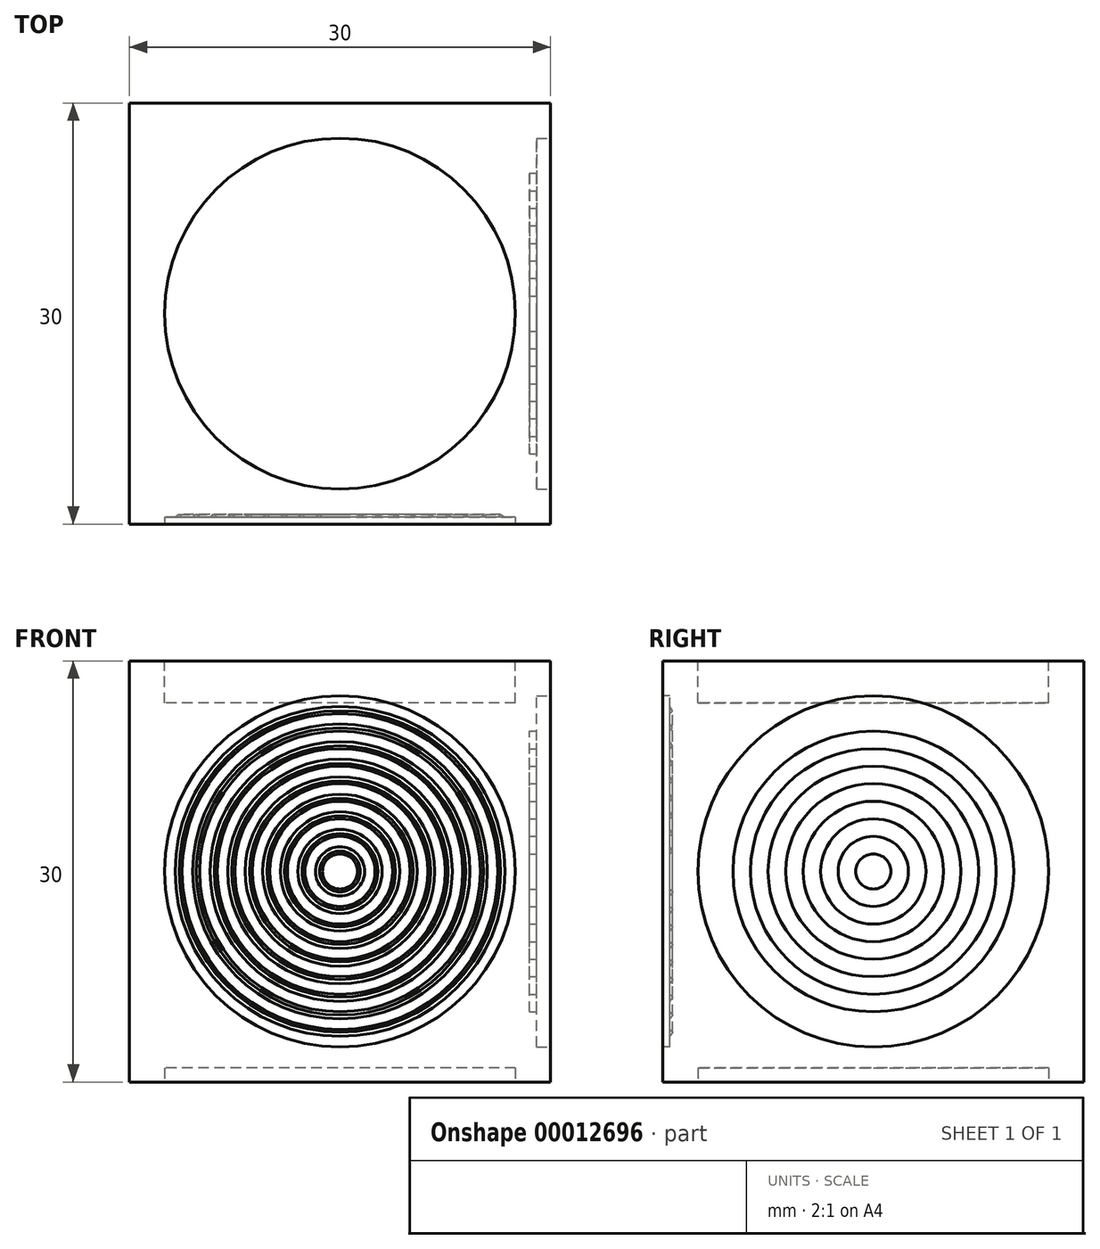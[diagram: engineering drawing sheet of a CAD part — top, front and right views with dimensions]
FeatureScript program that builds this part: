
annotation { "Feature Type Name" : "Feature", "Feature Type Description" : "" }
export const myFeature = defineFeature(function(context is Context, id is Id, definition is map)
    precondition{}
    {
        {
            var Q0;
            Q0=qCreatedBy(makeId("Top.planeOp"),FACE);
            var sketch = newSketch(context, id + "F0", { "sketchPlane" : qUnion([Q0])});
            skLineSegment(sketch, "E0.bottom", {"start": v(-30, 0) * mm, "end": v(0, 0) * mm});
            skLineSegment(sketch, "E0.top", {"start": v(-30, 30) * mm, "end": v(0, 30) * mm});
            skLineSegment(sketch, "E0.left", {"start": v(-30, 0) * mm, "end": v(-30, 30) * mm});
            skLineSegment(sketch, "E0.right", {"start": v(0, 0) * mm, "end": v(0, 30) * mm});
            skSolve(sketch);
        }
        {
            var Q0;
            Q0 = qSketchRegion(id + "F0", true);
            extrude(context, id + "F1", {"entities" : qUnion([Q0]), "depth" : 30 * mm});
        }
        {
            var Q0;
            Q0=qCreatedBy(makeId("Top.planeOp"),FACE);
            var sketch = newSketch(context, id + "F2", { "sketchPlane" : qUnion([Q0])});
            skCircle(sketch, "E1", {"center": v(-15, 15) * mm, "radius": 12.5 * mm});
            skSolve(sketch);
        }
        {
            var Q0;
            Q0=makeQuery(id+"F2.imprint","IMPRINT",FACE,{"disambiguationData":[TD([[makeQuery(id+"F2.imprint","IMPRINT",EDGE,{"derivedFrom":sQuery(id+"F2.wireOp",EDGE,"E1")}),1.0]])]});
            extrude(context, id + "F3", {"entities" : qUnion([Q0]), "operationType" : NewBodyOperationType.REMOVE, "depth" : 1 * mm});
        }
        {
            var Q0;
            Q0=makeQuery(id+"F1.opExtrude","CAP_FACE",FACE,{"disambiguationData":[OSD([sQuery(id+"F0.wireOp",EDGE,"E0.bottom"),sQuery(id+"F0.wireOp",EDGE,"E0.top"),sQuery(id+"F0.wireOp",EDGE,"E0.left"),sQuery(id+"F0.wireOp",EDGE,"E0.right")])],"isStart":false});
            var sketch = newSketch(context, id + "F4", { "sketchPlane" : qUnion([Q0])});
            skCircle(sketch, "E2", {"center": v(-15, 15) * mm, "radius": 12.5 * mm});
            skSolve(sketch);
        }
        {
            var Q0;
            Q0=makeQuery(id+"F4.imprint","IMPRINT",FACE,{"disambiguationData":[TD([[makeQuery(id+"F4.imprint","IMPRINT",EDGE,{"derivedFrom":sQuery(id+"F4.wireOp",EDGE,"E2")}),1.0]])]});
            extrude(context, id + "F5", {"entities" : qUnion([Q0]), "operationType" : NewBodyOperationType.REMOVE, "oppositeDirection" : true, "depth" : 3 * mm});
        }
        {
            var Q0;
            Q0=makeQuery(id+"F1.opExtrude","SWEPT_FACE",FACE,{"disambiguationData":[OSD([sQuery(id+"F0.wireOp",EDGE,"E0.bottom")])]});
            var sketch = newSketch(context, id + "F6", { "sketchPlane" : qUnion([Q0])});
            skSolve(sketch);
        }
        {
            var Q0;
            Q0=makeQuery(id+"F1.opExtrude","SWEPT_FACE",FACE,{"disambiguationData":[OSD([sQuery(id+"F0.wireOp",EDGE,"E0.right")])]});
            var sketch = newSketch(context, id + "F7", { "sketchPlane" : qUnion([Q0])});
            skCircle(sketch, "E3", {"center": v(15, 15) * mm, "radius": 12.5 * mm});
            skSolve(sketch);
        }
        {
            var Q0;
            Q0=makeQuery(id+"F7.imprint","IMPRINT",FACE,{"disambiguationData":[TD([[makeQuery(id+"F7.imprint","IMPRINT",EDGE,{"derivedFrom":sQuery(id+"F7.wireOp",EDGE,"E3")}),1.0]])]});
            var Q1;
            Q1=sQuery(id+"F7.wireOp",EDGE,"E3");
            extrude(context, id + "F8", {"entities" : qUnion([Q0]), "operationType" : NewBodyOperationType.REMOVE, "surfaceEntities" : qUnion([Q1]), "oppositeDirection" : true, "depth" : 1 * mm});
        }
        {
            var Q0;
            Q0=makeQuery(id+"F8.boolean.opBoolean","COPY",FACE,{"derivedFrom":makeQuery(id+"F8.opExtrude","CAP_FACE",FACE,{"disambiguationData":[OSD([sQuery(id+"F7.wireOp",EDGE,"E3")])],"isStart":false})});
            var sketch = newSketch(context, id + "F9", { "sketchPlane" : qUnion([Q0])});
            skCircle(sketch, "E4", {"center": v(15, 15) * mm, "radius": 5 * mm});
            skCircle(sketch, "E5", {"center": v(15, 15) * mm, "radius": 7.5 * mm});
            skCircle(sketch, "E6", {"center": v(15, 15) * mm, "radius": 10 * mm});
            skCircle(sketch, "E7", {"center": v(15, 15) * mm, "radius": 6.25 * mm});
            skCircle(sketch, "E8", {"center": v(15, 15) * mm, "radius": 2.5 * mm});
            skCircle(sketch, "E9", {"center": v(15, 15) * mm, "radius": 8.75 * mm});
            skCircle(sketch, "E10", {"center": v(15, 15) * mm, "radius": 3.75 * mm});
            skCircle(sketch, "E11", {"center": v(15, 15) * mm, "radius": 11.25 * mm});
            skCircle(sketch, "E12", {"center": v(15, 15) * mm, "radius": 1.25 * mm});
            skSolve(sketch);
        }
        {
            var Q0;
            Q0=makeQuery(id+"F9.imprint","IMPRINT",FACE,{"disambiguationData":[TD([[makeQuery(id+"F9.imprint","IMPRINT",EDGE,{"derivedFrom":sQuery(id+"F9.wireOp",EDGE,"E8")}),1.0]])]});
            var Q1;
            Q1=makeQuery(id+"F9.imprint","IMPRINT",FACE,{"disambiguationData":[TD([[makeQuery(id+"F9.imprint","IMPRINT",EDGE,{"derivedFrom":sQuery(id+"F9.wireOp",EDGE,"E4")}),1.0]])]});
            var Q2;
            Q2=makeQuery(id+"F9.imprint","IMPRINT",FACE,{"disambiguationData":[TD([[makeQuery(id+"F9.imprint","IMPRINT",EDGE,{"derivedFrom":sQuery(id+"F9.wireOp",EDGE,"E5")}),1.0]])]});
            var Q3;
            Q3=makeQuery(id+"F9.imprint","IMPRINT",FACE,{"disambiguationData":[TD([[makeQuery(id+"F9.imprint","IMPRINT",EDGE,{"derivedFrom":sQuery(id+"F9.wireOp",EDGE,"E6")}),1.0]])]});
            extrude(context, id + "F10", {"entities" : qUnion([Q0, Q1, Q2, Q3]), "operationType" : NewBodyOperationType.REMOVE, "oppositeDirection" : true, "depth" : .5 * mm});
        }
        {
            var Q0;
            {var subQ0=sQuery(id+"F0.wireOp",EDGE,"E0.bottom");Q0=makeQuery(id+"F6.imprint","IMPRINT",FACE,{"disambiguationData":[TD([[makeQuery(id+"F6.imprint","IMPRINT",EDGE,{"derivedFrom":makeQuery(id+"F1.opExtrude","CAP_EDGE",EDGE,{"disambiguationData":[OSD([subQ0])],"isStart":true})}),1.0]])]});}
            var sketch = newSketch(context, id + "F11", { "sketchPlane" : qUnion([Q0])});
            skCircle(sketch, "E13", {"center": v(-15, 15) * mm, "radius": 12.5 * mm});
            skSolve(sketch);
        }
        {
            var Q0;
            Q0 = qSketchRegion(id + "F11", true);
            extrude(context, id + "F12", {"entities" : qUnion([Q0]), "operationType" : NewBodyOperationType.REMOVE, "oppositeDirection" : true, "depth" : .5 * mm});
        }
        {
            var Q0;
            Q0=qCreatedBy(makeId("Top.planeOp"),FACE);
            cPlane(context, id + "F13", {"entities" : qUnion([Q0]), "cplaneType" : CPlaneType.OFFSET, "offset" : 15 * mm, "width" : 152.4 * mm, "height" : 152.4 * mm});
        }
        {
            var Q0;
            Q0=qCreatedBy(id+"F13.planeOp",FACE);
            var sketch = newSketch(context, id + "F14", { "sketchPlane" : qUnion([Q0])});
            skLineSegment(sketch, "E14", {"start": v(0, 0) * mm, "end": v(-15, 0) * mm, "construction": true});
            skLineSegment(sketch, "E15", {"start": v(-15, 2.5) * mm, "end": v(-15, 0) * mm, "construction": true});
            skLineSegment(sketch, "E16.0", {"start": v(-3.25, 0.5) * mm, "end": v(-3.75, 0.5) * mm});
            skPoint(sketch, "E17", {"position": v(-8.75, 0.5) * mm});
            skPoint(sketch, "E18", {"position": v(-10, 0.5) * mm});
            skPoint(sketch, "E19", {"position": v(-6.25, 0.5) * mm});
            skPoint(sketch, "E20", {"position": v(-11.25, 0.5) * mm});
            skPoint(sketch, "E21", {"position": v(-7.5, 0.5) * mm});
            skPoint(sketch, "E22", {"position": v(-12.5, 0.5) * mm});
            skPoint(sketch, "E23", {"position": v(-5, 0.5) * mm});
            skPoint(sketch, "E24", {"position": v(-13.75, 0.5) * mm});
            skPoint(sketch, "E25", {"position": v(-3.75, 0.5) * mm});
            skPoint(sketch, "E26", {"position": v(-13.25, 0.5) * mm});
            skPoint(sketch, "E27", {"position": v(-12, 0.5) * mm});
            skPoint(sketch, "E28", {"position": v(-10.75, 0.5) * mm});
            skPoint(sketch, "E29", {"position": v(-9.5, 0.5) * mm});
            skPoint(sketch, "E30", {"position": v(-8.25, 0.5) * mm});
            skPoint(sketch, "E31", {"position": v(-7, 0.5) * mm});
            skPoint(sketch, "E32", {"position": v(-5.75, 0.5) * mm});
            skPoint(sketch, "E33", {"position": v(-4.5, 0.5) * mm});
            skPoint(sketch, "E34", {"position": v(-3.25, 0.5) * mm});
            skPoint(sketch, "E35", {"position": v(-13.55, 0.7) * mm});
            skPoint(sketch, "E36", {"position": v(-12.3, 0.7) * mm});
            skPoint(sketch, "E37", {"position": v(-11.05, 0.7) * mm});
            skPoint(sketch, "E38", {"position": v(-9.8, 0.7) * mm});
            skPoint(sketch, "E39", {"position": v(-8.55, 0.7) * mm});
            skPoint(sketch, "E40", {"position": v(-7.3, 0.7) * mm});
            skPoint(sketch, "E41", {"position": v(-6.05, 0.7) * mm});
            skPoint(sketch, "E42", {"position": v(-4.77, 0.7) * mm});
            skPoint(sketch, "E43", {"position": v(-3.55, 0.7) * mm});
            skLineSegment(sketch, "E44", {"start": v(-13.75, 0.5) * mm, "end": v(-13.55, 0.7) * mm});
            skLineSegment(sketch, "E45", {"start": v(-13.55, 0.7) * mm, "end": v(-13.25, 0.5) * mm});
            skLineSegment(sketch, "E46", {"start": v(-12.5, 0.5) * mm, "end": v(-12.3, 0.7) * mm});
            skLineSegment(sketch, "E47", {"start": v(-12.3, 0.7) * mm, "end": v(-12, 0.5) * mm});
            skLineSegment(sketch, "E48", {"start": v(-11.25, 0.5) * mm, "end": v(-11.05, 0.7) * mm});
            skLineSegment(sketch, "E49", {"start": v(-10.75, 0.5) * mm, "end": v(-11.05, 0.7) * mm});
            skLineSegment(sketch, "E50", {"start": v(-10, 0.5) * mm, "end": v(-9.8, 0.7) * mm});
            skLineSegment(sketch, "E51", {"start": v(-9.5, 0.5) * mm, "end": v(-9.8, 0.7) * mm});
            skLineSegment(sketch, "E52", {"start": v(-8.75, 0.5) * mm, "end": v(-8.55, 0.7) * mm});
            skLineSegment(sketch, "E53", {"start": v(-8.25, 0.5) * mm, "end": v(-8.55, 0.7) * mm});
            skLineSegment(sketch, "E54", {"start": v(-7.5, 0.5) * mm, "end": v(-7.3, 0.7) * mm});
            skLineSegment(sketch, "E55", {"start": v(-7, 0.5) * mm, "end": v(-7.3, 0.7) * mm});
            skLineSegment(sketch, "E56", {"start": v(-6.25, 0.5) * mm, "end": v(-6.05, 0.7) * mm});
            skLineSegment(sketch, "E57", {"start": v(-5.75, 0.5) * mm, "end": v(-6.05, 0.7) * mm});
            skLineSegment(sketch, "E58", {"start": v(-5, 0.5) * mm, "end": v(-4.77, 0.7) * mm});
            skLineSegment(sketch, "E59", {"start": v(-4.5, 0.5) * mm, "end": v(-4.77, 0.7) * mm});
            skLineSegment(sketch, "E60", {"start": v(-3.75, 0.5) * mm, "end": v(-3.55, 0.7) * mm});
            skLineSegment(sketch, "E61", {"start": v(-3.25, 0.5) * mm, "end": v(-3.55, 0.7) * mm});
            skPoint(sketch, "E62.orphan", {"position": v(-2.5, 0.5) * mm});
            skLineSegment(sketch, "E63.trimOffspring", {"start": v(-4.5, 0.5) * mm, "end": v(-5, 0.5) * mm});
            skLineSegment(sketch, "E64.trimOffspring", {"start": v(-5.75, 0.5) * mm, "end": v(-6.25, 0.5) * mm});
            skLineSegment(sketch, "E65.trimOffspring", {"start": v(-7, 0.5) * mm, "end": v(-7.5, 0.5) * mm});
            skLineSegment(sketch, "E66.trimOffspring", {"start": v(-8.25, 0.5) * mm, "end": v(-8.75, 0.5) * mm});
            skLineSegment(sketch, "E67.trimOffspring", {"start": v(-9.5, 0.5) * mm, "end": v(-10, 0.5) * mm});
            skLineSegment(sketch, "E68.trimOffspring", {"start": v(-10.75, 0.5) * mm, "end": v(-11.25, 0.5) * mm});
            skLineSegment(sketch, "E69.trimOffspring", {"start": v(-12, 0.5) * mm, "end": v(-12.5, 0.5) * mm});
            skLineSegment(sketch, "E70.trimOffspring", {"start": v(-13.25, 0.5) * mm, "end": v(-13.75, 0.5) * mm});
            skPoint(sketch, "E71.orphan", {"position": v(-15, 0.5) * mm});
            skSolve(sketch);
        }
        {
            var Q0;
            Q0 = qSketchRegion(id + "F14", true);
            var Q1;
            Q1=sQuery(id+"F14.wireOp",EDGE,"E15");
            revolve(context, id + "F15", {"operationType" : NewBodyOperationType.REMOVE, "entities" : qUnion([Q0]), "axis" : qUnion([Q1]), "revolveType" : RevolveType.FULL, "oppositeDirection" : true});
        }
    });
